# Revit family: Electronics_Commercial-Audio_Biamp_Preamplifier_PM-4100
name_source: partatom
category: Communication Devices
units: mm (PartAtom-declared; Revit-internal decimal feet)

## family parameters
Cut with Voids When Loaded = No
Host = Face
Maintain Annotation Orientation = No
OmniClass Number = 23.85.10.11.14
Part Type = Normal
Room Calculation Point = No
Round Connector Dimension = Use Diameter
Shared = No

## types (1)
- PM-4100
    Altitude = 0-6,600 ft (0-2000m) MSL
    Apparent Load = 5 VA
    Compliance = FCC Part 15B (USA)
UL listed (USA and Canada)
CE Marked (Europe)
RoHS Directive (Europe)
    Connector Description = 12V DC 5W
    Cooling = Convection
    Default Elevation = 4' - 0"
    Depth = 0' - 2 3/4"
    Description = PM4100 Preamplifier
    Height = 0' - 1 15/32"
    Housing Material = Biamp - Metal - Black
    Humidity = 10-90% relative humidity (non-condensing)
    Manufacturer = Biamp
    Max Power Consumption = 5 W
    Model = PM4100
    Number of Poles = 1
    Power Factor = 1
    Product Documentation Link = https://downloads.biamp.com
    Product Page URL = https://www.biamp.com
    Product data url = https://www.bimobject.com
    Temperature Range = 32 - 86° F (0 – 30° C)
    URL = https://www.biamp.com
    Voltage = 12 V
    Weight = 1.10 lbf
    Width = 0' - 8 19/32"

## geometry (parser evidence)
native form markers: Sweep x3
no freeform markers — native parametric forms only
